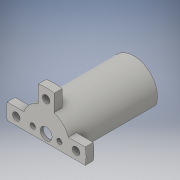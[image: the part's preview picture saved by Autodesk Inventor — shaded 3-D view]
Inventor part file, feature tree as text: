
AUTODESK INVENTOR PART (.ipt)
format: ipt  version: 2016 (Build 200138000, 138)  size: 159,744 bytes
history: native  units: in
note: dims shown in document units (in); Inventor stores cm internally (conversion verified against a paired STEP export)
features: extrude x4, sketch x4
ambient origin geometry x8: Origin, YZ Plane, XZ Plane, XY Plane, X Axis, Y Axis, Z Axis, Center Point
bodies: Solid1 (feature_tree)
feature tree (8):
  extrude  "Extrusion1"  Depth=1.184in
  extrude  "Extrusion2"  Depth=0.335in
  extrude  "Extrusion3"  Depth=0.075in TaperAngle=0.0deg
  extrude  "Extrusion4"  Depth=0.2in
  sketch  "Sketch1"  dims[d0=0.295in d1=1.184in]
  sketch  "Sketch3"  dims[d2=0.13in d3=0.335in]
  sketch  "Sketch4"  dims[d4=0.335in d5=0.075in d6=0.0in]
  sketch  "Sketch5"  dims[d7=0.2in d8=1.184in d9=0.984in d10=0.2in d11=2.125in d12=0.0in d13=1.6534in d14=1.184in d18=0.05in d19=0.3in d20=0.2in d21=0.2in d22=1.0in d23=1.0in d24=1.0in d25=0.4in d27=0.4in d29=0.2in d30=0.0in d31=0.1875in d32=0.75in d33=0.75in d34=0.75in d37=0.15in d38=0.0in]
